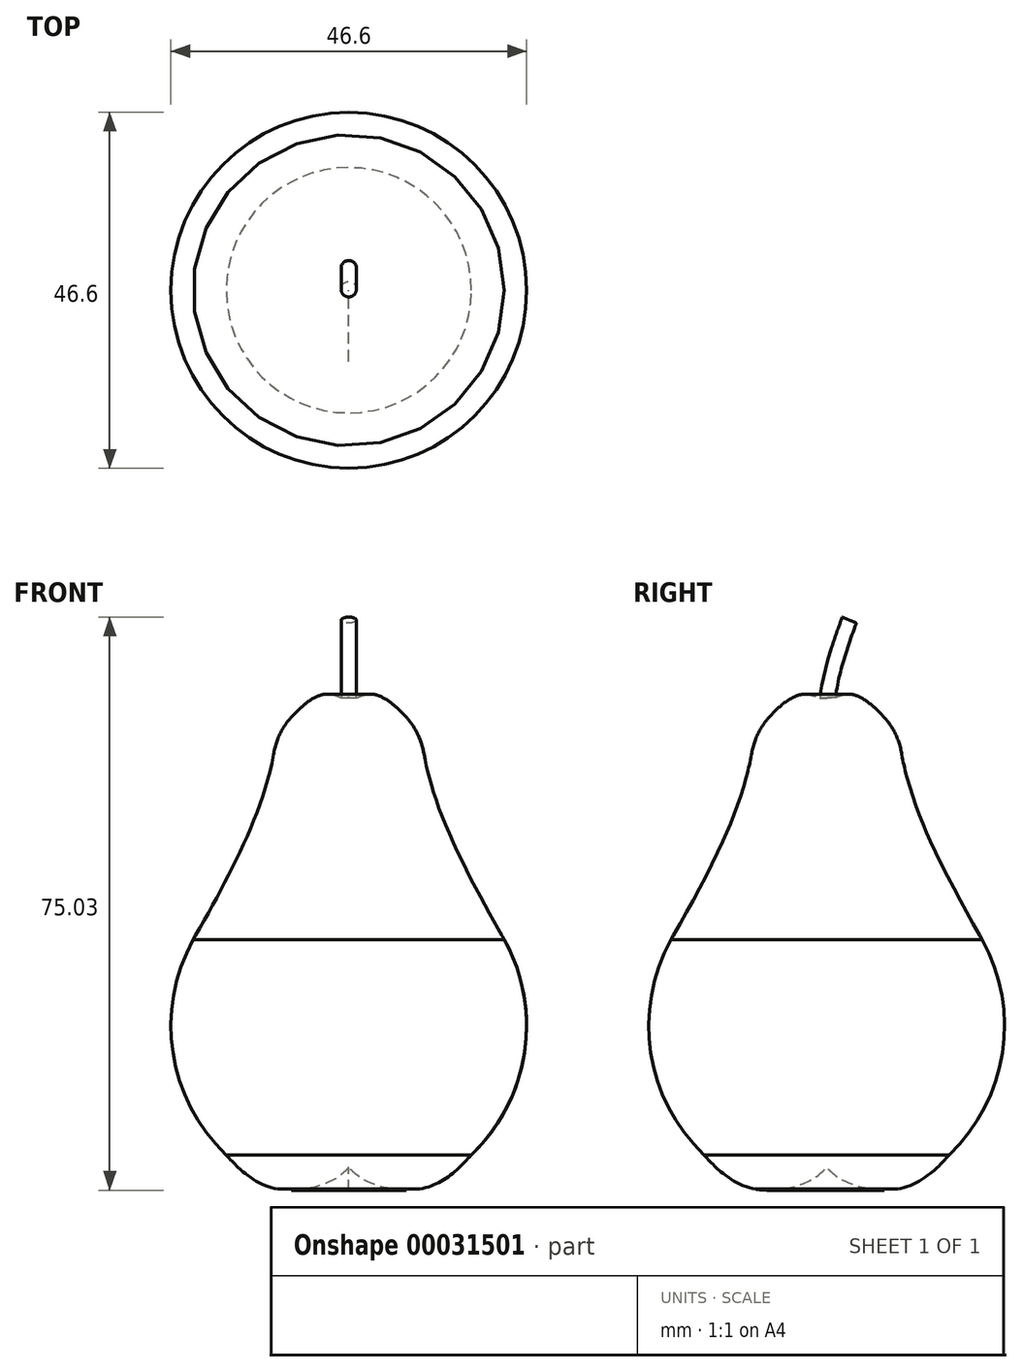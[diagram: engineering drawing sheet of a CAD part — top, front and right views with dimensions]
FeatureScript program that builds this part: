
annotation { "Feature Type Name" : "Feature", "Feature Type Description" : "" }
export const myFeature = defineFeature(function(context is Context, id is Id, definition is map)
    precondition{}
    {
        {
            var Q0;
            Q0=qCreatedBy(makeId("Right.planeOp"),FACE);
            var sketch = newSketch(context, id + "F0", { "sketchPlane" : qUnion([Q0])});
            skCircle(sketch, "E0", {"center": v(0, -18.53) * mm, "radius": 23.3 * mm});
            skCircle(sketch, "E1", {"center": v(0, 15.38) * mm, "radius": 9.98 * mm});
            skFitSpline(sketch, "E2", {"points": [v(-9.86, 16.98) * mm, v(-12.87, 7.3) * mm, v(-20.37, -7.23) * mm], "startDerivative": vector(-2.55, -15.18) * mm, "endDerivative": vector(-11.26, -19.63) * mm});
            skLineSegment(sketch, "E3", {"start": v(0, 25.37) * mm, "end": v(0, -41.83) * mm});
            skFitSpline(sketch, "E4", {"points": [v(-20.47, -29.66) * mm, v(-16.06, -35.42) * mm, v(-9.3, -39.9) * mm, v(0, -37) * mm], "startDerivative": vector(16.48, -22.15) * mm, "endDerivative": vector(14.6, 19.1) * mm});
            skFitSpline(sketch, "E5", {"points": [v(-9.86, 16.98) * mm, v(-8.76, 20.17) * mm, v(-6.14, 23.26) * mm, v(-3.06, 24.89) * mm, v(0, 23.92) * mm], "startDerivative": vector(3.3, 13.24) * mm, "endDerivative": vector(12.86, -6.48) * mm});
            skSolve(sketch);
        }
        {
            var Q0;
            {var subQ1=sQuery(id+"F0.wireOp",EDGE,"E1");var subQ4=makeQuery(id+"F0.imprint","INTERSECT",VERTEX,{"derivedFrom":[subQ1,sQuery(id+"F0.wireOp",EDGE,"E2")]});Q0=makeQuery(id+"F0.imprint","IMPRINT",FACE,{"disambiguationData":[TD([[makeQuery(id+"F0.imprint","IMPRINT",EDGE,{"disambiguationData":[TD([[subQ4,1.0]])],"derivedFrom":subQ1}),1.0]])]});}
            var Q1;
            {var subQ1=sQuery(id+"F0.wireOp",EDGE,"E0");var subQ4=sQuery(id+"F0.wireOp",EDGE,"E2");var subQ5=makeQuery(id+"F0.imprint","INTERSECT",VERTEX,{"disambiguationData":[OD(1.0)],"derivedFrom":[subQ1,subQ4]});Q1=makeQuery(id+"F0.imprint","IMPRINT",FACE,{"disambiguationData":[TD([[makeQuery(id+"F0.imprint","IMPRINT",EDGE,{"disambiguationData":[TD([[subQ5,1.0]])],"derivedFrom":subQ1}),1.0]])]});}
            var Q2;
            {var subQ0=sQuery(id+"F0.wireOp",EDGE,"E4");var subQ1=sQuery(id+"F0.wireOp",EDGE,"E0");var subQ3=makeQuery(id+"F0.imprint","INTERSECT",VERTEX,{"disambiguationData":[OD(0.0)],"derivedFrom":[subQ1,subQ0]});Q2=makeQuery(id+"F0.imprint","IMPRINT",FACE,{"disambiguationData":[TD([[makeQuery(id+"F0.imprint","IMPRINT",EDGE,{"disambiguationData":[TD([[subQ3,-1.0]])],"derivedFrom":subQ1}),1.0]])]});}
            var Q3;
            {var subQ0=sQuery(id+"F0.wireOp",EDGE,"E4");var subQ1=sQuery(id+"F0.wireOp",EDGE,"E0");var subQ3=makeQuery(id+"F0.imprint","INTERSECT",VERTEX,{"disambiguationData":[OD(1.0)],"derivedFrom":[subQ1,subQ0]});Q3=makeQuery(id+"F0.imprint","IMPRINT",FACE,{"disambiguationData":[TD([[makeQuery(id+"F0.imprint","IMPRINT",EDGE,{"disambiguationData":[TD([[subQ3,-1.0]])],"derivedFrom":subQ1}),-1.0]])]});}
            var Q4;
            {var subQ3=sQuery(id+"F0.wireOp",EDGE,"E0");var subQ5=sQuery(id+"F0.wireOp",EDGE,"E2");var subQ6=makeQuery(id+"F0.imprint","INTERSECT",VERTEX,{"disambiguationData":[OD(1.0)],"derivedFrom":[subQ3,subQ5]});Q4=makeQuery(id+"F0.imprint","IMPRINT",FACE,{"disambiguationData":[TD([[makeQuery(id+"F0.imprint","IMPRINT",EDGE,{"disambiguationData":[TD([[subQ6,1.0]])],"derivedFrom":subQ3}),-1.0]])]});}
            var Q5;
            {var subQ0=sQuery(id+"F0.wireOp",EDGE,"E5");var subQ1=sQuery(id+"F0.wireOp",EDGE,"E1");var subQ3=makeQuery(id+"F0.imprint","INTERSECT",VERTEX,{"disambiguationData":[OD(0.0)],"derivedFrom":[subQ1,subQ0]});Q5=makeQuery(id+"F0.imprint","IMPRINT",FACE,{"disambiguationData":[TD([[makeQuery(id+"F0.imprint","IMPRINT",EDGE,{"disambiguationData":[TD([[subQ3,-1.0]])],"derivedFrom":subQ1}),-1.0]])]});}
            var Q6;
            {var subQ0=sQuery(id+"F0.wireOp",EDGE,"E5");var subQ1=sQuery(id+"F0.wireOp",EDGE,"E1");var subQ2=makeQuery(id+"F0.imprint","INTERSECT",VERTEX,{"disambiguationData":[OD(3.0)],"derivedFrom":[subQ1,subQ0]});Q6=makeQuery(id+"F0.imprint","IMPRINT",FACE,{"disambiguationData":[TD([[makeQuery(id+"F0.imprint","IMPRINT",EDGE,{"disambiguationData":[TD([[subQ2,-1.0]])],"derivedFrom":subQ1}),1.0]])]});}
            var Q7;
            {var subQ0=sQuery(id+"F0.wireOp",EDGE,"E5");var subQ1=sQuery(id+"F0.wireOp",EDGE,"E1");var subQ2=makeQuery(id+"F0.imprint","INTERSECT",VERTEX,{"disambiguationData":[OD(0.0)],"derivedFrom":[subQ1,subQ0]});Q7=makeQuery(id+"F0.imprint","IMPRINT",FACE,{"disambiguationData":[TD([[makeQuery(id+"F0.imprint","IMPRINT",EDGE,{"disambiguationData":[TD([[subQ2,-1.0]])],"derivedFrom":subQ1}),1.0]])]});}
            var Q8;
            Q8=sQuery(id+"F0.wireOp",EDGE,"E3");
            revolve(context, id + "F1", {"entities" : qUnion([Q0, Q1, Q2, Q3, Q4, Q5, Q6, Q7]), "axis" : qUnion([Q8]), "revolveType" : RevolveType.FULL});
        }
        {
            var Q0;
            Q0=qCreatedBy(makeId("Top.planeOp"),FACE);
            cPlane(context, id + "F2", {"entities" : qUnion([Q0]), "cplaneType" : CPlaneType.OFFSET, "offset" : 19.05 * mm, "width" : 152.4 * mm, "height" : 152.4 * mm});
        }
        {
            var Q0;
            Q0=qCreatedBy(id+"F2.planeOp",FACE);
            var sketch = newSketch(context, id + "F3", { "sketchPlane" : qUnion([Q0])});
            skCircle(sketch, "E6", {"center": v(0, 0) * mm, "radius": 1 * mm});
            skSolve(sketch);
        }
        {
            var Q0;
            Q0=qCreatedBy(makeId("Right.planeOp"),FACE);
            var sketch = newSketch(context, id + "F4", { "sketchPlane" : qUnion([Q0])});
            skFitSpline(sketch, "E7", {"points": [v(0, 19.05) * mm, v(0, 23) * mm, v(0.96, 28.52) * mm, v(2.97, 34.6) * mm], "startDerivative": vector(-0.51, 12.6) * mm, "endDerivative": vector(5.96, 16.33) * mm});
            skSolve(sketch);
        }
        {
            var Q0;
            Q0=makeQuery(id+"F3.imprint","IMPRINT",FACE,{"disambiguationData":[TD([[makeQuery(id+"F3.imprint","IMPRINT",EDGE,{"derivedFrom":sQuery(id+"F3.wireOp",EDGE,"E6")}),1.0]])]});
            var Q1;
            Q1=sQuery(id+"F4.wireOp",EDGE,"E7");
            sweep(context, id + "F5", {"operationType" : NewBodyOperationType.ADD, "profiles" : qUnion([Q0]), "path" : qUnion([Q1])});
        }
    });
